# Revit family: 2Torneira de parede para lavatorio LEED - Pressmatic 120 - DocolMatic
name_source: partatom
category: Conexões hidráulicas
revit_build: Autodesk Revit MEP 2014 (Build: 20131024_2115(x64)
units: mm (PartAtom-declared; Revit-internal decimal feet)

## types (1)
- 1/2" e 3/4"
    Acessório = Sim
    Conexão CW = Sim
    Conexão HW = Sim
    Conexão de resíduos = Sim
    Conexão de ventilação = Sim
    Descrição = Torneira de parede 1/2" e 3/4" para lavatório LEED, Pressmatic 120 - DocolMatic
    Diâmetro Nominal = 20  [stored 0.0656168 ft]
    Docol: Acabamento = Cromado
    Docol: Ambiente = Banheiro
    Docol: Bitola = 1/2" e 3/4"
    Docol: Categoria = Torneiras
    Docol: Código = 00595806
    Docol: Descrição = Torneira de parede 1/2" e 3/4" para lavatório LEED, Pressmatic 120 - DocolMatic
    Docol: Fabricante = Docol
    Docol: Linha = Produtos sugeridos para LEED
    Docol: Link do Produto = https://www.docol.com.br
    Docol: Temperatura Máxima = 40 °C
    Elevação-padrão = 500  [stored 1.64042 ft]
    Fabricante = Docol
    H = 148.158
    Modelo = 00595806
    Raio Canopla = 5.99
    Raio Nominal = 10  [stored 0.0328084 ft]
    Raio Saida = 14  [stored 0.0459318 ft]
    Raio Torneira = 17.25  [stored 0.0565945 ft]
    Saida Angulo = 20.00°
    Saida Comprimento = 28  [stored 0.0918635 ft]
    Saida X = 36
    Saida Y = 113.5  [stored 0.372375 ft]
    Tampa = 135.357
    URL = www.docol.com.br

note: [stored X ft] marks values corroborated as IEEE doubles in the binary element streams (Revit-internal decimal feet)

## geometry (parser evidence)
native form markers: Sweep x1
no freeform markers — native parametric forms only
